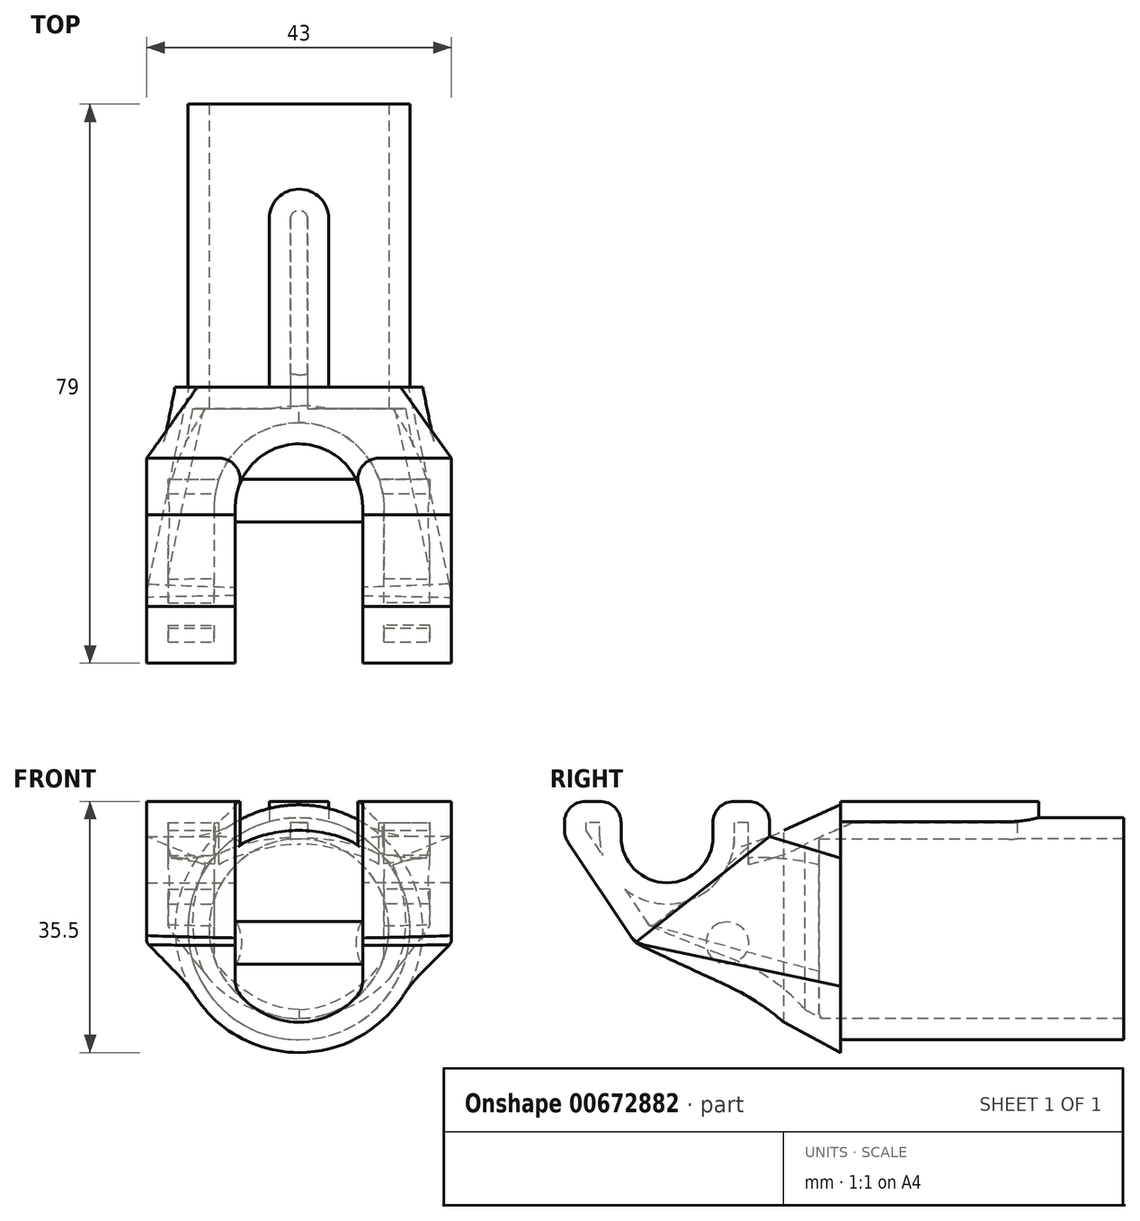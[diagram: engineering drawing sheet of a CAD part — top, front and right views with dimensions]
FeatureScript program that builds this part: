
annotation { "Feature Type Name" : "Feature", "Feature Type Description" : "" }
export const myFeature = defineFeature(function(context is Context, id is Id, definition is map)
    precondition{}
    {
        {
            var Q0;
            Q0=qCreatedBy(makeId("Front.planeOp"),FACE);
            var sketch = newSketch(context, id + "F0", { "sketchPlane" : qUnion([Q0])});
            skArc(sketch, "E0", {"start": v(0, -15.7) * mm, "mid": v(15.7, 0) * mm, "end": v(0, 15.7) * mm});
            skLineSegment(sketch, "E1", {"start": v(0, 15.7) * mm, "end": v(0, -15.7) * mm});
            skSolve(sketch);
        }
        {
            var Q0;
            Q0=qSketchRegion(id+"F0",true);
            extrude(context, id + "F1", {"entities" : qUnion([Q0]), "oppositeDirection" : true, "depth" : 40 * mm, "offsetDistance" : 25 * mm});
        }
        {
            var Q0;
            Q0=qCreatedBy(makeId("Top.planeOp"),FACE);
            var sketch = newSketch(context, id + "F2", { "sketchPlane" : qUnion([Q0])});
            skLineSegment(sketch, "E2.bottom", {"start": v(0, 0) * mm, "end": v(4.2, 0) * mm});
            skLineSegment(sketch, "E2.right", {"start": v(4.2, 0) * mm, "end": v(4.2, 23.8) * mm});
            skArc(sketch, "E3", {"start": v(4.2, 23.8) * mm, "mid": v(2.97, 26.77) * mm, "end": v(0, 28) * mm});
            skLineSegment(sketch, "E4", {"start": v(0, 28) * mm, "end": v(0, 0) * mm});
            skSolve(sketch);
        }
        {
            var Q0;
            Q0=qSketchRegion(id+"F2",true);
            extrude(context, id + "F3", {"entities" : qUnion([Q0]), "operationType" : NewBodyOperationType.ADD, "depth" : 18 * mm, "offsetDistance" : 25 * mm});
        }
        {
            var Q0;
            Q0=qCreatedBy(makeId("Front.planeOp"),FACE);
            var sketch = newSketch(context, id + "F4", { "sketchPlane" : qUnion([Q0])});
            skArc(sketch, "E5", {"start": v(0, -17.5) * mm, "mid": v(17.5, 0) * mm, "end": v(0, 17.5) * mm});
            skLineSegment(sketch, "E6.bottom", {"start": v(0, 10) * mm, "end": v(14.36, 10) * mm, "construction": true});
            skLineSegment(sketch, "E6.top", {"start": v(0, -10) * mm, "end": v(14.36, -10) * mm, "construction": true});
            skLineSegment(sketch, "E6.right", {"start": v(14.36, 10) * mm, "end": v(14.36, -10) * mm, "construction": true});
            skLineSegment(sketch, "E7", {"start": v(0, 17.5) * mm, "end": v(0, -17.5) * mm});
            skPoint(sketch, "E7.endSnap0", {"position": v(0, -10) * mm});
            skSolve(sketch);
        }
        {
            var Q0;
            Q0=qCreatedBy(makeId("Right.planeOp"),FACE);
            var sketch = newSketch(context, id + "F5", { "sketchPlane" : qUnion([Q0])});
            skLineSegment(sketch, "E8", {"start": v(-31, 13) * mm, "end": v(-31, 18) * mm});
            skLineSegment(sketch, "E9", {"start": v(-31, 18) * mm, "end": v(-39, 18) * mm});
            skLineSegment(sketch, "E10", {"start": v(-10, 13) * mm, "end": v(-10, 18) * mm});
            skLineSegment(sketch, "E11", {"start": v(-10, 18) * mm, "end": v(-18, 18) * mm});
            skLineSegment(sketch, "E12", {"start": v(-18, 18) * mm, "end": v(-18, 13) * mm});
            skArc(sketch, "E13", {"start": v(-31, 13) * mm, "mid": v(-24.5, 6.5) * mm, "end": v(-18, 13) * mm});
            skLineSegment(sketch, "E14", {"start": v(-39, 18) * mm, "end": v(-39, 13) * mm});
            skLineSegment(sketch, "E15", {"start": v(-39, 13) * mm, "end": v(-29, -2) * mm});
            skLineSegment(sketch, "E16", {"start": v(-29, -2) * mm, "end": v(-10, 13) * mm});
            skSolve(sketch);
        }
        {
            var Q0;
            Q0=qSketchRegion(id+"F5",true);
            extrude(context, id + "F6", {"entities" : qUnion([Q0]), "depth" : 21.5 * mm, "offsetDistance" : 25 * mm});
        }
        {
            var Q0;
            Q0=makeQuery(id+"F6.opExtrude","SWEPT_FACE",FACE,{"disambiguationData":[OSD([sQuery(id+"F5.wireOp",EDGE,"E16")])]});
            var Q1;
            Q1=makeQuery(id+"F4.imprint","IMPRINT",FACE,{"disambiguationData":[TD([[makeQuery(id+"F4.imprint","IMPRINT",EDGE,{"derivedFrom":sQuery(id+"F4.wireOp",EDGE,"E5")}),1.0]])]});
            var Q2;
            Q2=sQuery(id+"F4.wireOp",VERTEX,"E6.right.start");
            var Q3;
            Q3=makeQuery(id+"F6.opExtrude","CAP_VERTEX",VERTEX,{"disambiguationData":[OSD([sQuery(id+"F5.wireOp",EDGE,"E10"),sQuery(id+"F5.wireOp",EDGE,"E16")])],"isStart":false});
            loft(context, id + "F7", {"sheetProfilesArray" : [{ "sheetProfileEntities" : qUnion([Q0]) }, { "sheetProfileEntities" : qUnion([Q1]) }], "matchConnections" : true, "connections" : [{ "connectionEntities" : qUnion([Q2, Q3]), "connectionEdgeQueries" : qUnion([]), "connectionEdgeParameters" : [] }]});
        }
        {
            var Q0;
            Q0=makeQuery(id+"F1.opExtrude","SWEPT_BODY",BODY,{"disambiguationData":[OSD([sQuery(id+"F0.wireOp",EDGE,"E0")])]});
            var Q1;
            Q1=makeQuery(id+"F6.opExtrude","SWEPT_BODY",BODY,{"disambiguationData":[OSD([sQuery(id+"F5.wireOp",EDGE,"E8"),sQuery(id+"F5.wireOp",EDGE,"E9"),sQuery(id+"F5.wireOp",EDGE,"E10"),sQuery(id+"F5.wireOp",EDGE,"E11"),sQuery(id+"F5.wireOp",EDGE,"E12"),sQuery(id+"F5.wireOp",EDGE,"E13"),sQuery(id+"F5.wireOp",EDGE,"E14"),sQuery(id+"F5.wireOp",EDGE,"E15"),sQuery(id+"F5.wireOp",EDGE,"E16")])]});
            var Q2;
            Q2=makeQuery(id+"F7.opLoft","SWEPT_BODY",BODY,{"disambiguationData":[OSD([makeQuery(id+"F4.imprint","IMPRINT",FACE,{"disambiguationData":[TD([[makeQuery(id+"F4.imprint","IMPRINT",EDGE,{"derivedFrom":sQuery(id+"F4.wireOp",EDGE,"E5")}),1.0]])]}),sQuery(id+"F5.wireOp",EDGE,"E16")])]});
            booleanBodies(context, id + "F8", {"operationType" : BooleanOperationType.UNION, "tools" : qUnion([Q0, Q1, Q2])});
        }
        {
            var Q0;
            Q0=qCreatedBy(makeId("Top.planeOp"),FACE);
            var sketch = newSketch(context, id + "F9", { "sketchPlane" : qUnion([Q0])});
            skLineSegment(sketch, "E17", {"start": v(0, -50) * mm, "end": v(9, -50) * mm});
            skLineSegment(sketch, "E18", {"start": v(9, -50) * mm, "end": v(9, -17) * mm});
            skArc(sketch, "E19", {"start": v(9, -17) * mm, "mid": v(6.36, -10.64) * mm, "end": v(0, -8) * mm});
            skLineSegment(sketch, "E20", {"start": v(0, -8) * mm, "end": v(0, -50) * mm});
            skSolve(sketch);
        }
        {
            var Q0;
            Q0=qSketchRegion(id+"F9",true);
            extrude(context, id + "F10", {"entities" : qUnion([Q0]), "operationType" : NewBodyOperationType.REMOVE, "endBound" : BoundingType.THROUGH_ALL, "oppositeDirection" : true, "depth" : 25 * mm, "offsetDistance" : 25 * mm, "hasSecondDirection" : true, "secondDirectionBound" : SecondDirectionBoundingType.THROUGH_ALL, "secondDirectionOppositeDirection" : false, "secondDirectionDepth" : 25 * mm});
        }
        {
            var Q0;
            Q0=qCreatedBy(makeId("Right.planeOp"),FACE);
            var sketch = newSketch(context, id + "F11", { "sketchPlane" : qUnion([Q0])});
            skCircle(sketch, "E21", {"center": v(-16, -2) * mm, "radius": 3 * mm});
            skSolve(sketch);
        }
        {
            var Q0;
            Q0=makeQuery(id+"F6.opExtrude","SWEPT_EDGE",EDGE,{"disambiguationData":[OSD([sQuery(id+"F5.wireOp",EDGE,"E9"),sQuery(id+"F5.wireOp",EDGE,"E14")])]});
            var Q1;
            Q1=makeQuery(id+"F6.opExtrude","SWEPT_EDGE",EDGE,{"disambiguationData":[OSD([sQuery(id+"F5.wireOp",EDGE,"E8"),sQuery(id+"F5.wireOp",EDGE,"E9")])]});
            var Q2;
            Q2=makeQuery(id+"F6.opExtrude","SWEPT_EDGE",EDGE,{"disambiguationData":[OSD([sQuery(id+"F5.wireOp",EDGE,"E11"),sQuery(id+"F5.wireOp",EDGE,"E12")])]});
            var Q3;
            Q3=makeQuery(id+"F6.opExtrude","SWEPT_EDGE",EDGE,{"disambiguationData":[OSD([sQuery(id+"F5.wireOp",EDGE,"E10"),sQuery(id+"F5.wireOp",EDGE,"E11")])]});
            var Q4;
            Q4=makeQuery(id+"F10.boolean.opBoolean","INTERSECT",EDGE,{"derivedFrom":[makeQuery(id+"F6.opExtrude","SWEPT_FACE",FACE,{"disambiguationData":[OSD([sQuery(id+"F5.wireOp",EDGE,"E10")])]}),makeQuery(id+"F10.opExtrude","SWEPT_FACE",FACE,{"disambiguationData":[OSD([sQuery(id+"F9.wireOp",EDGE,"E19")])]})]});
            var Q5;
            Q5=makeQuery(id+"F6.opExtrude","SWEPT_EDGE",EDGE,{"disambiguationData":[OSD([sQuery(id+"F5.wireOp",EDGE,"E14"),sQuery(id+"F5.wireOp",EDGE,"E15")])]});
            var Q6;
            {var subQ0=sQuery(id+"F5.wireOp",EDGE,"E16");var subQ1=sQuery(id+"F5.wireOp",EDGE,"E15");Q6=makeQuery(id+"F8.opBoolean","MERGE",EDGE,{"derivedFrom":[makeQuery(id+"F6.opExtrude","SWEPT_EDGE",EDGE,{"disambiguationData":[OSD([subQ1,subQ0])]}),makeQuery(id+"F7.opLoft","MID_CAP_EDGE",EDGE,{"disambiguationData":[OSD([subQ1,subQ0])],"capPos":0.0})]});}
            fillet(context, id + "F12", {"entities" : qUnion([Q0, Q1, Q2, Q3, Q4, Q5, Q6]), "radius" : 3 * mm, "tangentPropagation" : true, "allowEdgeOverflow" : false});
        }
        {
            var Q0;
            Q0=makeQuery(id+"F1.opExtrude","SWEPT_BODY",BODY,{"disambiguationData":[OSD([sQuery(id+"F0.wireOp",EDGE,"E0"),sQuery(id+"F0.wireOp",EDGE,"E1")])]});
            var Q1;
            Q1=qCreatedBy(makeId("Right.planeOp"),FACE);
            mirror(context, id + "F13", {"operationType" : NewBodyOperationType.ADD, "entities" : qUnion([Q0]), "mirrorPlane" : qUnion([Q1])});
        }
        {
            var Q0;
            {var subQ0=makeQuery(id+"F1.opExtrude","CAP_FACE",FACE,{"disambiguationData":[OSD([sQuery(id+"F0.wireOp",EDGE,"E0"),sQuery(id+"F0.wireOp",EDGE,"E1")])],"isStart":false});Q0=makeQuery(id+"F13.boolean.opBoolean","MERGE",FACE,{"derivedFrom":[subQ0,makeQuery(id+"F13.opPattern","COPY",FACE,{"derivedFrom":subQ0,"instanceName":"1"})]});}
            shell(context, id + "F14", {"entities" : qUnion([Q0]), "thickness" : 3 * mm});
        }
        {
            var Q0;
            Q0=qSketchRegion(id+"F11",true);
            var Q1;
            Q1=makeQuery(id+"F10.boolean.opBoolean","COPY",FACE,{"derivedFrom":makeQuery(id+"F10.opExtrude","SWEPT_FACE",FACE,{"disambiguationData":[OSD([sQuery(id+"F9.wireOp",EDGE,"E18")])]})});
            var Q2;
            Q2=makeQuery(id+"F13.opPattern","COPY",FACE,{"derivedFrom":makeQuery(id+"F10.boolean.opBoolean","COPY",FACE,{"derivedFrom":makeQuery(id+"F10.opExtrude","SWEPT_FACE",FACE,{"disambiguationData":[OSD([sQuery(id+"F9.wireOp",EDGE,"E18")])]})}),"instanceName":"1"});
            extrude(context, id + "F15", {"entities" : qUnion([Q0]), "operationType" : NewBodyOperationType.ADD, "endBound" : BoundingType.UP_TO_SURFACE, "depth" : 25 * mm, "endBoundEntityFace" : qUnion([Q1]), "offsetDistance" : 25 * mm, "hasSecondDirection" : true, "secondDirectionBound" : SecondDirectionBoundingType.UP_TO_SURFACE, "secondDirectionOppositeDirection" : true, "secondDirectionDepth" : 25 * mm, "secondDirectionBoundEntityFace" : qUnion([Q2])});
        }
    });
